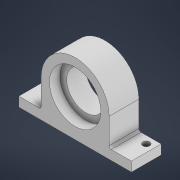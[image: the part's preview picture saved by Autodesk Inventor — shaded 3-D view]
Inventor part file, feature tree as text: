
AUTODESK INVENTOR PART (.ipt)
format: ipt  version: 2021 (Build 250183000, 183)  size: 314,880 bytes
history: native  units: mm
features: extrude x6, sketch x6, fillet x2
ambient origin geometry x8: Origin, YZ Plane, XZ Plane, XY Plane, X Axis, Y Axis, Z Axis, Center Point
bodies: Volumenkörper1 (feature_tree)
feature tree (14):
  extrude  "Extrusion1"  Depth=32.0mm
  sketch  "Skizze2"  dims[d2=24.2mm d3=14.0mm d4=0.0mm]
  extrude  "Extrusion2"  Depth=14.0mm TaperAngle=0.0deg
  extrude  "Extrusion3"  Depth=3.0mm
  extrude  "Extrusion4"  Depth=10.5mm TaperAngle=0.0deg
  fillet  "Rundung1"  Radius=24.2mm
  extrude  "Extrusion5"  Depth=9.0mm TaperAngle=0.0deg
  fillet  "Rundung2"  Radius=16.0mm
  extrude  "Extrusion6"  Depth=1.0mm
  sketch  "Skizze1"  dims[d0=32.0mm d1=32.0mm]
  sketch  "Skizze3"  dims[d5=3.0mm d6=3.0mm]
  sketch  "Skizze4"  dims[d7=10.5mm d8=0.0mm d9=10.5mm d10=0.0mm d11=24.2mm]
  sketch  "Skizze5"  dims[d12=18.0mm d13=9.0mm d14=0.0mm d15=16.0mm]
  sketch  "Skizze6"  dims[d16=3.2mm d17=3.5mm d18=3.5mm d19=3.2mm d20=3.5mm d21=3.5mm d22=5.0mm d23=0.0mm d24=1.0mm d25=3.2mm d26=3.2mm d27=1.5mm d28=0.0mm]
